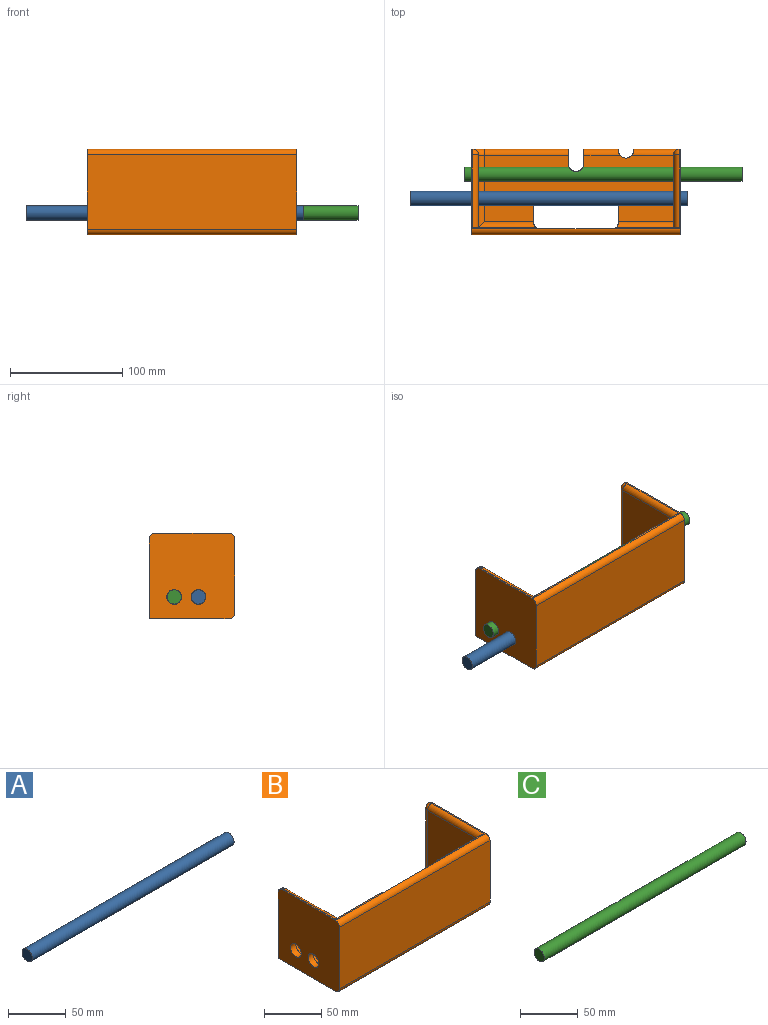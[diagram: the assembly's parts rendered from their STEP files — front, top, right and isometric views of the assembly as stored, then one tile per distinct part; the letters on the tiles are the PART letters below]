
ASSEMBLY  parts=3 mates=2
PART A: 3 faces, bbox 247.7x12.7x12.7 mm
  f0: cylinder r=6.35mm len=247.65mm, axis (1,0,0), area 9880.8mm2, adj f1,f2
  f1: plane 12.7x12.7mm, normal (-1,0,0), area 126.7mm2, adj f0
  f2: plane 12.7x12.7mm, normal (1,0,0), area 126.7mm2, adj f0
PART B: 47 faces, bbox 190.2x76.2x79.7 mm
  f0: sphere r=5.08mm, area 40.5mm2, adj f3,f13,f14
  f1: sphere r=5.08mm, area 40.5mm2, adj f8,f15,f16
  f2: torus R=10.16mm, axis (0,1,0), area 86.8mm2, adj f3,f9,f17,f23
  f3: cylinder r=5.08mm len=59.69mm, axis (0,0,1), area 476.3mm2, adj f0,f2,f12,f23
  f4: cylinder r=6.6mm len=13.21mm, axis (1,0,0), area 263.5mm2, adj f12,f24
  f5: cylinder r=6.6mm len=13.21mm, axis (1,0,0), area 263.5mm2, adj f12,f24
  f6: cylinder r=6.6mm len=13.21mm, axis (-1,0,0), area 263.5mm2, adj f18,f25
  f7: cylinder r=6.6mm len=13.21mm, axis (-1,0,0), area 263.5mm2, adj f18,f25
  f8: cylinder r=5.08mm len=69.85mm, axis (0,0,-1), area 531.6mm2, adj f1,f11,f18,f26
  f9: cylinder r=5.08mm len=74.94mm, axis (1,0,0), area 598mm2, adj f2,f22,f23,f34
  f10: cylinder r=5.08mm len=31.95mm, axis (1,0,0), area 245.4mm2, adj f20,f34,f35,f36
  f11: cylinder r=5.08mm len=42.12mm, axis (1,0,0), area 300.7mm2, adj f8,f26,f34,f35
  f12: plane 64.77x59.69mm, normal (1,0,0), area 3592.1mm2, adj f3,f4,f5,f14,f17,f33
  f13: cylinder r=5.08mm len=5.08mm, axis (1,0,0), area 10.1mm2, adj f0,f23,f24,f30
  f14: cylinder r=5.08mm len=64.77mm, axis (0,-1,0), area 516.8mm2, adj f0,f12,f30,f33
  f15: cylinder r=5.08mm len=64.77mm, axis (0,1,0), area 516.8mm2, adj f1,f18,f29,f31
  f16: cylinder r=5.08mm len=5.08mm, axis (1,0,0), area 10.1mm2, adj f1,f25,f26,f29
  f17: cylinder r=5.08mm len=64.77mm, axis (0,1,0), area 502.1mm2, adj f2,f12,f32,f34
  f18: plane 64.77x64.77mm, normal (-1,0,0), area 3915.6mm2, adj f6,f7,f8,f15,f27,f31,f34
  f19: plane 186.71x66.04mm, normal (0,-1,0), area 12330.4mm2, adj f24,f25,f28,f38
  f20: plane 12.7x6.35mm, normal (-1,0,0), area 75.1mm2, adj f10,f21,f34,f36,f37
  f21: cylinder r=6.99mm len=13.97mm, axis (0,0,-1), area 139.3mm2, adj f20,f22,f34,f37
  f22: plane 12.7x6.35mm, normal (1,0,0), area 75.1mm2, adj f9,f21,f23,f34,f37
  f23: plane 86.37x71.12mm, normal (0,1,0), area 220.6mm2, adj f2,f3,f9,f13,f22,f24,f37
  f24: plane 76.2x76.2mm, normal (-1,0,0), area 5515.8mm2, adj f4,f5,f13,f19,f23,f28,f30,f37
  f25: plane 76.2x76.2mm, normal (1,0,0), area 5515.8mm2, adj f6,f7,f16,f19,f26,f28,f29,f37
  f26: plane 71.12x41.97mm, normal (0,1,0), area 142mm2, adj f8,f11,f16,f25,f35,f37
  f27: cylinder r=5.08mm len=51.13mm, axis (-1,0,0), area 399.9mm2, adj f18,f31,f34,f41,f46
  f28: cylinder r=5.08mm len=186.71mm, axis (-1,0,0), area 1489.9mm2, adj f19,f24,f25,f29,f30,f45
  f29: plane 66.04x60.84mm, normal (0,0,1), area 156.6mm2, adj f15,f16,f25,f28,f31,f46
  f30: plane 66.04x60.84mm, normal (0,0,1), area 156.6mm2, adj f13,f14,f24,f28,f33,f44
  f31: plane 64.77x56.21mm, normal (0,1,0), area 3317.5mm2, adj f15,f18,f27,f29,f46
  f32: cylinder r=5.08mm len=51.13mm, axis (-1,0,0), area 385.2mm2, adj f17,f33,f34,f43,f44
  f33: plane 64.77x56.21mm, normal (0,1,0), area 3317.5mm2, adj f12,f14,f30,f32,f44
  f34: plane 168.93x59.69mm, normal (0,0,1), area 7923.8mm2, adj f9,f10,f11,f17,f18,f20,f21,f22
  f35: cylinder r=6.99mm len=13.97mm, axis (0,0,1), area 138.2mm2, adj f10,f11,f26,f34,f36,f37
  f36: plane 30.52x1.27mm, normal (0,1,0), area 38.8mm2, adj f10,f20,f35,f37
  f37: plane 186.71x71.12mm, normal (0,0,-1), area 10515mm2, adj f20,f21,f22,f23,f24,f25,f26,f35
  f38: cylinder r=5.08mm len=186.71mm, axis (1,0,0), area 1489.9mm2, adj f19,f24,f25,f37,f45
  f39: plane 65.02x6.35mm, normal (0,-1,0), area 412.9mm2, adj f34,f37,f40,f42
  f40: cylinder r=5.08mm len=6.35mm, axis (0,0,-1), area 50.7mm2, adj f34,f37,f39,f41
  f41: plane 22.35x6.51mm, normal (-1,0,0), area 142mm2, adj f27,f34,f37,f40,f46
  f42: cylinder r=5.08mm len=6.35mm, axis (0,0,-1), area 50.7mm2, adj f34,f37,f39,f43
  f43: plane 22.35x6.51mm, normal (1,0,0), area 142mm2, adj f32,f34,f37,f42,f44
  f44: cylinder r=5.08mm len=76.2mm, axis (0,0,-1), area 313.9mm2, adj f30,f32,f33,f37,f43,f45
  f45: plane 76.2x65.02mm, normal (0,1,0), area 4954.8mm2, adj f28,f38,f44,f46
  f46: cylinder r=5.08mm len=76.2mm, axis (0,0,-1), area 313.9mm2, adj f27,f29,f31,f37,f41,f45
PART C: 4 faces, bbox 247.7x12.7x12.7 mm
  f0: cylinder r=6.35mm len=247.65mm, axis (-1,0,0), area 9730.7mm2, adj f1,f2,f3
  f1: plane 12.7x12.7mm, normal (1,0,0), area 126.7mm2, adj f0
  f2: plane 12.7x12.7mm, normal (-1,0,0), area 126.7mm2, adj f0
  f3: cylinder r=6.99mm len=12.49mm, axis (0,0,-1), area 147.5mm2, adj f0
PLACE A t=(0,-80.52,15.24)mm
PLACE B t=(0,-80.52,15.24)mm fixed
PLACE C t=(0,-80.52,15.24)mm
MATE slider C.f0 <-> B.f4  axis (-1,0,0) through (24.12,-102.7,85.47)mm
MATE slider A.f0 <-> B.f6  axis (1,0,0) through (-24.12,-124.37,85.47)mm
